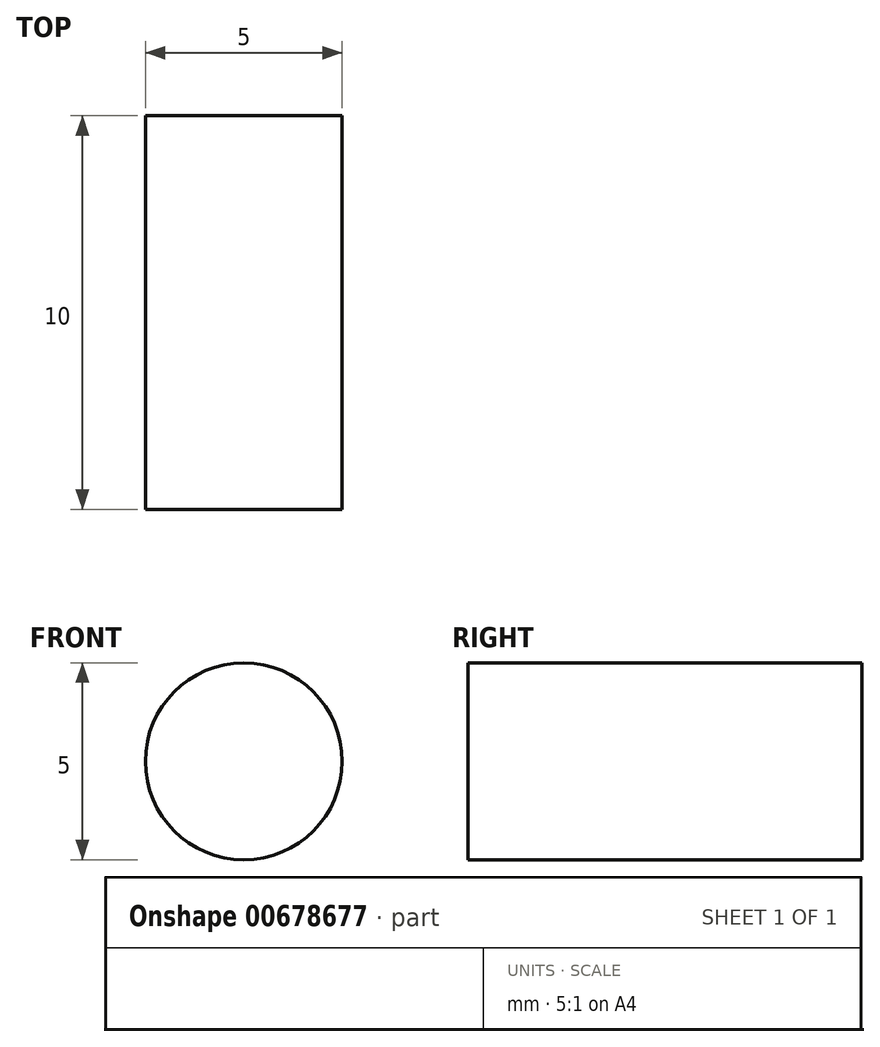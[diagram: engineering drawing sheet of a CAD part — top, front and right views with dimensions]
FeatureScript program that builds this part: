
annotation { "Feature Type Name" : "Feature", "Feature Type Description" : "" }
export const myFeature = defineFeature(function(context is Context, id is Id, definition is map)
    precondition{}
    {
        {
            var Q0;
            Q0=qCreatedBy(makeId("Front.planeOp"),FACE);
            var sketch = newSketch(context, id + "F0", { "sketchPlane" : qUnion([Q0])});
            skCircle(sketch, "E0", {"center": v(0, 0.08) * mm, "radius": 2.5 * mm});
            skSolve(sketch);
        }
        {
            var Q0;
            Q0 = qSketchRegion(id + "F0", true);
            extrude(context, id + "F1", {"entities" : qUnion([Q0]), "depth" : 10 * mm, "offsetDistance" : 25.4 * mm});
        }
    });
